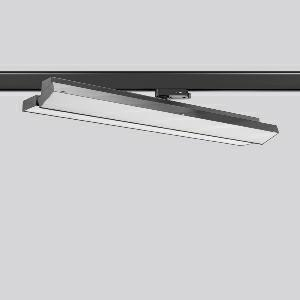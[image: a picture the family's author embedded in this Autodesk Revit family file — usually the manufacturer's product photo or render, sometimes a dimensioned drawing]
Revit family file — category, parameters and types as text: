
# Revit family: tx-move_742164_003_2_76_84ba
name_source: partatom
category: Lighting Fixtures
units: mm (PartAtom-declared; Revit-internal decimal feet)

## family parameters
Cut with Voids When Loaded = No
Host = Face
Light Source = No
Part Type = Normal
Room Calculation Point = No
Round Connector Dimension = Use Diameter
Shared = No

## types (1)
- MultiLumen 1 (1 x LED Modul 927, 1775 lm, 2700)
    Apparent Load = 38 VA
    CIE Flux Codes = 47 79 96 100 100
    Color Rendering = 92
    Color Temperature = 2700
    Default Elevation = 1800 mm
    Description = Series: TX-MOVE
Multifunctional surface-mounted spotlight for area lighting. Very flat design. Housing: sheet steel, powder-coated. Rotation range: 356°. Swivel range: 90°. Consistent alignment possible with visible tilt scale. High-efficiency LED units with flush-mounted opal diffuser made of non-yellowing PMMA. Symmetrical wide beam light distribution. Best colour rendering with CRI >90 for fresh products and coloured textiles. With adapter for RZB 3-circuit DALI tracks. Suitable for Track on ceiling. MultiLumen: Luminous flux adjustable in 3 steps. Factory setting is the highest luminous flux. Environmentally friendly and resource-saving due to replaceable and recyclable components. 
Colour: deep black, matt (RAL 9005)
Length: 570 mm
Width: 119 mm
Height: 88 mm
Lamp: LED
Socket: without socket
Colour temperature: 2700K
Colour rendering index (CRI): 90
System power: 38 W
Rated luminous flux: 3550 lm
Luminous efficiency: 93 lm/W
System power 2: 51 W
Rated luminous flux 2: 4650 lm
Luminous efficiency 2: 91 lm/W
System power 3: 62 W
Rated luminous flux 3: 5500 lm
Luminous efficiency 3: 89 lm/W
Control gear: Dimmable EVG, DALI
Protection class: I
Type of protection: IP 20
    Height = 75 mm
    Lamp = 1 x LED Modul 927
    Lamp Light Flux = 1775 lm
    Lamp count = 1
    Length = 569 mm
    Lifetime = 50000 h
    Luminous efficacy = 93 lm/W
    Manufacturer = RZB
    ModVariant = No
    Model = 742164.003.2.76
    Mounting Place = Ceiling
    Mounting Type = Surface mounted
    Number of Poles = 1
    OnlyDefault = Yes
    Power Factor = 1
    Product Name = TX-MOVE
    Product group = Track mounted projectors
    ProductGroupID = 301
    Protection Class = Protection class I
    Protection Degree = IP 20
    RLX_Detail_Level = 1
    RLX_Emergency_Light_Flux = 0 lm
    RLX_Emergency_Type = 0
    RLX_Emergency_Type_DB = No
    RlxData = <blob elided: 35749 chars, md5=66f61fdc>
    Socket = socket
    Standby Power = 0 W
    System Light Flux = 3550 lm
    System Power = 38 W
    Type Comments = MultiLumen 1
    Type Image = 742164.003.jpg
    URL = http://relux.com
    VarID = multilumen_1
    Voltage = 0 V
    Weight = 0.00 kg
    Width = 119 mm

## geometry (parser evidence)
native form markers: Blend x4, Sweep x15
no freeform markers — native parametric forms only
